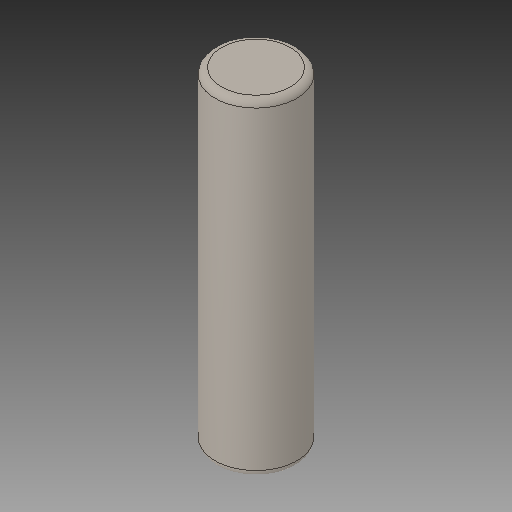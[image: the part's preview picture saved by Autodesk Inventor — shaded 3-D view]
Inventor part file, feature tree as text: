
AUTODESK INVENTOR PART (.ipt)
format: ipt  version: 2018 (Build 220112000, 112)  size: 93,184 bytes
history: native  units: in
note: dims shown in document units (in); Inventor stores cm internally (conversion verified against a paired STEP export)
features: revolve x1
ambient origin geometry x8: Origin, YZ Plane, XZ Plane, XY Plane, X Axis, Y Axis, Z Axis, Center Point
bodies: Solid1 (feature_tree)
feature tree (1):
  revolve  "Revolve1"  [1 undecoded]
note: 1 required parameter value undecoded (feature->parameter linkage not recoverable at this tier; creation-order binding heuristic only, values carry confidence <= 0.55)
